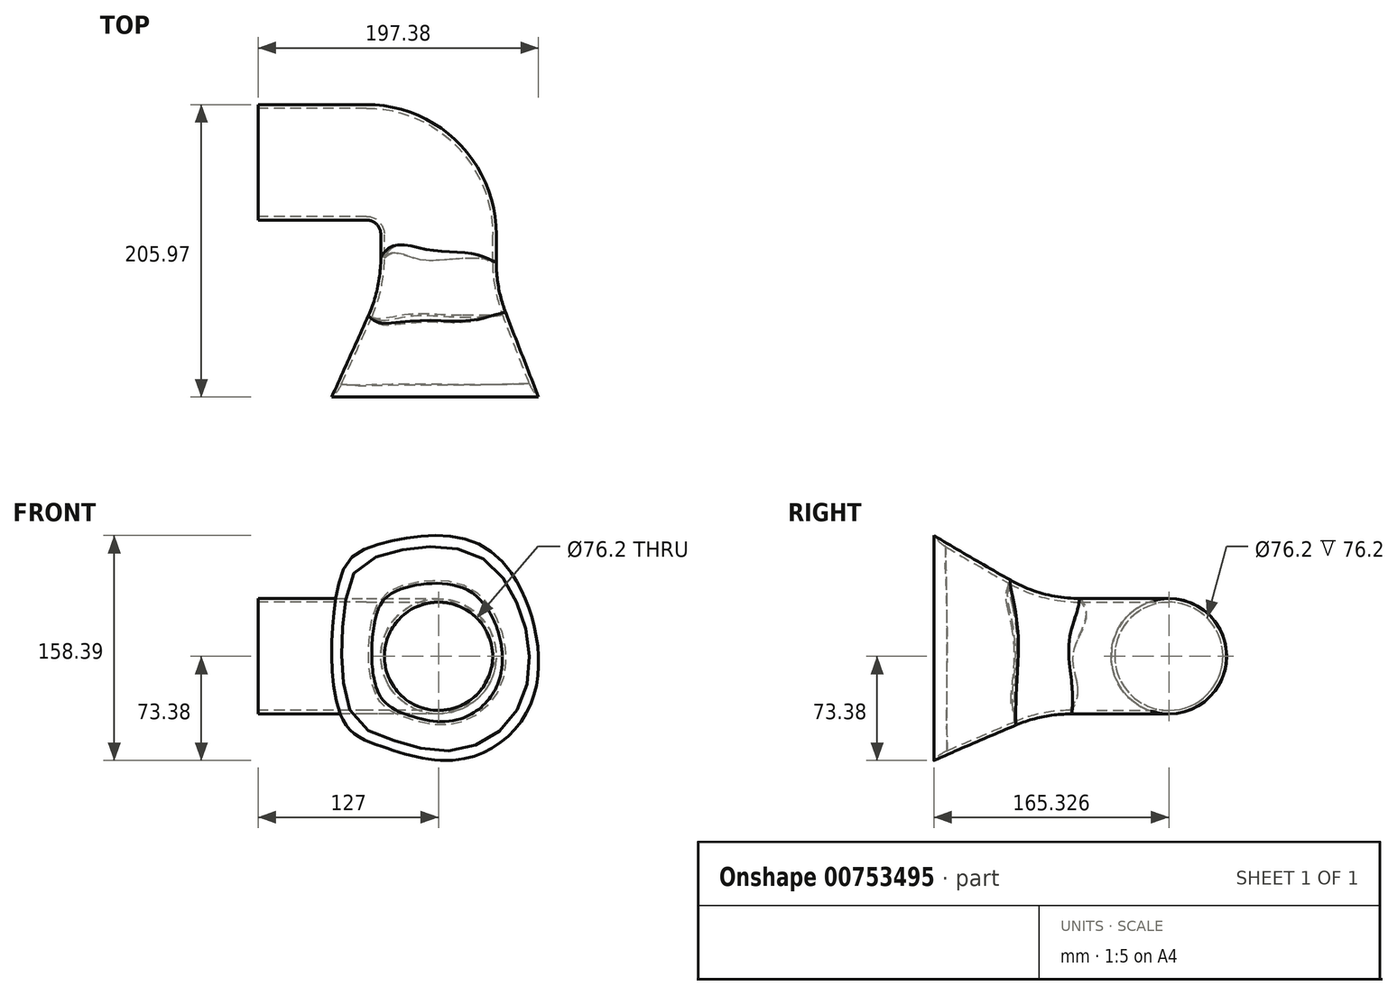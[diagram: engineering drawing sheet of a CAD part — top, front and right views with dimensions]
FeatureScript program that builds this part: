
annotation { "Feature Type Name" : "Feature", "Feature Type Description" : "" }
export const myFeature = defineFeature(function(context is Context, id is Id, definition is map)
    precondition{}
    {
        {
            var Q0;
            Q0=qCreatedBy(makeId("Front.planeOp"),FACE);
            var sketch = newSketch(context, id + "F0", { "sketchPlane" : qUnion([Q0])});
            skFitSpline(sketch, "E0", {"points": [v(-66.49, -39.83) * mm, v(-66.49, 54.14) * mm, v(-52.26, 71.8) * mm, v(-18.21, 80.86) * mm, v(38.68, 68.8) * mm, v(65.4, -23.45) * mm, v(16.7, -69.57) * mm, v(-38.9, -60.95) * mm, v(-66.49, -39.83) * mm]});
            skSolve(sketch);
        }
        {
            var Q0;
            Q0=qCreatedBy(makeId("Front.planeOp"),FACE);
            cPlane(context, id + "F1", {"entities" : qUnion([Q0]), "cplaneType" : CPlaneType.OFFSET, "offset" : 76.2 * mm, "oppositeDirection" : true, "width" : 152.4 * mm, "height" : 152.4 * mm});
        }
        {
            var Q0;
            Q0=qCreatedBy(id+"F1.planeOp",FACE);
            var sketch = newSketch(context, id + "F2", { "sketchPlane" : qUnion([Q0])});
            skCircle(sketch, "E1", {"center": v(0, 0) * mm, "radius": 38.1 * mm});
            skSolve(sketch);
        }
        {
            var Q0;
            Q0=makeQuery(id+"F0.imprint","IMPRINT",FACE,{"disambiguationData":[TD([[makeQuery(id+"F0.imprint","IMPRINT",EDGE,{"derivedFrom":sQuery(id+"F0.wireOp",EDGE,"E0")}),-1.0]])]});
            var Q1;
            Q1=makeQuery(id+"F2.imprint","IMPRINT",FACE,{"disambiguationData":[TD([[makeQuery(id+"F2.imprint","IMPRINT",EDGE,{"derivedFrom":sQuery(id+"F2.wireOp",EDGE,"E1")}),1.0]])]});
            loft(context, id + "F3", {"sheetProfilesArray" : [{ "sheetProfileEntities" : qUnion([Q0]) }, { "sheetProfileEntities" : qUnion([Q1]) }]});
        }
        {
            var Q0;
            Q0=qCreatedBy(makeId("Top.planeOp"),FACE);
            var sketch = newSketch(context, id + "F4", { "sketchPlane" : qUnion([Q0])});
            skLineSegment(sketch, "E2", {"start": v(0, 51.03) * mm, "end": v(0, 114.53) * mm});
            skArc(sketch, "E3", {"start": v(0, 114.53) * mm, "mid": v(-14.88, 150.45) * mm, "end": v(-50.8, 165.33) * mm});
            skLineSegment(sketch, "E4", {"start": v(-50.8, 165.33) * mm, "end": v(-127, 165.33) * mm});
            skSolve(sketch);
        }
        {
            var Q0;
            Q0=qCreatedBy(makeId("Right.planeOp"),FACE);
            cPlane(context, id + "F5", {"entities" : qUnion([Q0]), "cplaneType" : CPlaneType.OFFSET, "offset" : 114.3 * mm, "oppositeDirection" : true, "width" : 152.4 * mm, "height" : 152.4 * mm});
        }
        {
            var Q0;
            Q0=qCreatedBy(id+"F5.planeOp",FACE);
            var sketch = newSketch(context, id + "F6", { "sketchPlane" : qUnion([Q0])});
            skCircle(sketch, "E5", {"center": v(165.33, 0) * mm, "radius": 38.1 * mm});
            skSolve(sketch);
        }
        {
            var Q0;
            Q0=makeQuery(id+"F3.opLoft","CAP_FACE",FACE,{"disambiguationData":[OSD([makeQuery(id+"F2.imprint","IMPRINT",FACE,{"disambiguationData":[TD([[makeQuery(id+"F2.imprint","IMPRINT",EDGE,{"derivedFrom":sQuery(id+"F2.wireOp",EDGE,"E1")}),1.0]])]})])],"isStart":true});
            var Q1;
            Q1=makeQuery(id+"F6.imprint","IMPRINT",FACE,{"disambiguationData":[TD([[makeQuery(id+"F6.imprint","IMPRINT",EDGE,{"derivedFrom":sQuery(id+"F6.wireOp",EDGE,"E5")}),1.0]])]});
            var Q2;
            Q2=sQuery(id+"F4.wireOp",EDGE,"E2");
            var Q3;
            Q3=sQuery(id+"F4.wireOp",EDGE,"E3");
            var Q4;
            Q4=sQuery(id+"F4.wireOp",EDGE,"E4");
            sweep(context, id + "F7", {"operationType" : NewBodyOperationType.ADD, "profiles" : qUnion([Q0, Q1]), "path" : qUnion([Q2, Q3, Q4])});
        }
        {
            var Q0;
            Q0=makeQuery(id+"F7.boolean.opBoolean","SPLIT",EDGE,{"disambiguationData":[OD(2.0)],"derivedFrom":makeQuery(id+"F3.opLoft","MID_CAP_EDGE",EDGE,{"disambiguationData":[OSD([sQuery(id+"F2.wireOp",EDGE,"E1")])],"capPos":1.0})});
            var Q1;
            {var subQ0=sQuery(id+"F2.wireOp",EDGE,"E1");Q1=makeQuery(id+"F7.boolean.opBoolean","INTERSECT",EDGE,{"disambiguationData":[OD(0.0)],"derivedFrom":[makeQuery(id+"F3.opLoft","SWEPT_FACE",FACE,{"disambiguationData":[OSD([sQuery(id+"F0.wireOp",EDGE,"E0"),subQ0])]}),makeQuery(id+"F7.opSweep","SWEPT_FACE",FACE,{"disambiguationData":[OSD([subQ0,sQuery(id+"F4.wireOp",EDGE,"E2")])]})]});}
            var Q2;
            {var subQ0=sQuery(id+"F2.wireOp",EDGE,"E1");Q2=makeQuery(id+"F7.boolean.opBoolean","INTERSECT",EDGE,{"disambiguationData":[OD(1.0)],"derivedFrom":[makeQuery(id+"F3.opLoft","SWEPT_FACE",FACE,{"disambiguationData":[OSD([sQuery(id+"F0.wireOp",EDGE,"E0"),subQ0])]}),makeQuery(id+"F7.opSweep","SWEPT_FACE",FACE,{"disambiguationData":[OSD([subQ0,sQuery(id+"F4.wireOp",EDGE,"E2")])]})]});}
            var Q3;
            Q3=makeQuery(id+"F7.boolean.opBoolean","SPLIT",EDGE,{"disambiguationData":[OD(1.0)],"derivedFrom":makeQuery(id+"F3.opLoft","MID_CAP_EDGE",EDGE,{"disambiguationData":[OSD([sQuery(id+"F2.wireOp",EDGE,"E1")])],"capPos":1.0})});
            var Q4;
            {var subQ0=sQuery(id+"F2.wireOp",EDGE,"E1");Q4=makeQuery(id+"F7.boolean.opBoolean","INTERSECT",EDGE,{"disambiguationData":[OD(2.0)],"derivedFrom":[makeQuery(id+"F3.opLoft","SWEPT_FACE",FACE,{"disambiguationData":[OSD([sQuery(id+"F0.wireOp",EDGE,"E0"),subQ0])]}),makeQuery(id+"F7.opSweep","SWEPT_FACE",FACE,{"disambiguationData":[OSD([subQ0,sQuery(id+"F4.wireOp",EDGE,"E2")])]})]});}
            var Q5;
            {var subQ0=sQuery(id+"F2.wireOp",EDGE,"E1");Q5=makeQuery(id+"F7.boolean.opBoolean","INTERSECT",EDGE,{"disambiguationData":[OD(3.0)],"derivedFrom":[makeQuery(id+"F3.opLoft","SWEPT_FACE",FACE,{"disambiguationData":[OSD([sQuery(id+"F0.wireOp",EDGE,"E0"),subQ0])]}),makeQuery(id+"F7.opSweep","SWEPT_FACE",FACE,{"disambiguationData":[OSD([subQ0,sQuery(id+"F4.wireOp",EDGE,"E2")])]})]});}
            var Q6;
            Q6=makeQuery(id+"F7.boolean.opBoolean","SPLIT",EDGE,{"disambiguationData":[OD(3.0)],"derivedFrom":makeQuery(id+"F3.opLoft","MID_CAP_EDGE",EDGE,{"disambiguationData":[OSD([sQuery(id+"F2.wireOp",EDGE,"E1")])],"capPos":1.0})});
            fillet(context, id + "F8", {"entities" : qUnion([Q0, Q1, Q2, Q3, Q4, Q5, Q6]), "radius" : 101.6 * mm, "tangentPropagation" : true, "allowEdgeOverflow" : false});
        }
        {
            var Q0;
            Q0=makeQuery(id+"F7.opSweep","CAP_FACE",FACE,{"disambiguationData":[OSD([makeQuery(id+"F2.imprint","IMPRINT",FACE,{"disambiguationData":[TD([[makeQuery(id+"F2.imprint","IMPRINT",EDGE,{"derivedFrom":sQuery(id+"F2.wireOp",EDGE,"E1")}),1.0]])]}),sQuery(id+"F4.wireOp",VERTEX,"E4.end")])],"isStart":false});
            var Q1;
            Q1=makeQuery(id+"F3.opLoft","CAP_FACE",FACE,{"disambiguationData":[OSD([makeQuery(id+"F0.imprint","IMPRINT",FACE,{"disambiguationData":[TD([[makeQuery(id+"F0.imprint","IMPRINT",EDGE,{"derivedFrom":sQuery(id+"F0.wireOp",EDGE,"E0")}),-1.0]])]})])],"isStart":true});
            shell(context, id + "F9", {"entities" : qUnion([Q0, Q1]), "thickness" : 2.54 * mm, "oppositeDirection" : true});
        }
        {
            var Q0;
            Q0=makeQuery(id+"F9.opShell","OFFSET_EDGE",EDGE,{"disambiguationData":[OSD([sQuery(id+"F0.wireOp",EDGE,"E0")])]});
            fillet(context, id + "F10", {"entities" : qUnion([Q0]), "radius" : 25.4 * mm, "tangentPropagation" : true, "allowEdgeOverflow" : false});
        }
    });
